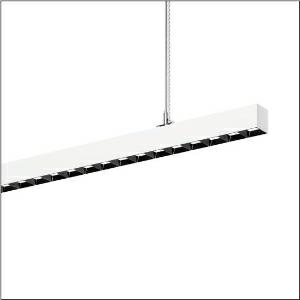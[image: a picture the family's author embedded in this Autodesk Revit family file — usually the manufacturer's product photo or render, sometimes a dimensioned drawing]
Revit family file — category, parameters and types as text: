
# Revit family: silica_r__21_51mx31dc4dwb_7dad
name_source: partatom
category: Lighting Fixtures
units: mm (PartAtom-declared; Revit-internal decimal feet)

## family parameters
Cut with Voids When Loaded = No
Host = Face
Light Source = No
Part Type = Normal
Room Calculation Point = No
Round Connector Dimension = Use Diameter
Shared = No

## types (1)
- --- (1 x LED, 18230 lm, 105.9 W, 4000K)
    Apparent Load = 106 VA
    CIE Flux Codes = 87 99 100 59 100
    Color Rendering = 80
    Color Temperature = 4000K
    Default Elevation = 1800 mm
    Description = Silica® 21, office luminaire, primary light control with darklight reflector, of PMMA, black, CAT 2 (L<= 3000cd/m²), light emission: direct/indirect distribution, primary light characteristic: symmetric, installation type: suspended mounting, LED, rated luminous flux: 18.230lm, luminous efficacy: 172lm/W, light colour: 840, colour temperature: 4000K, control gear: DALI 2, with terminal, 3+2-pole, max. 2.5mm², mains connection: 220..240V, AC, 50/60Hz, rated input power: 105.9W, luminaire housing, of aluminium, traffic white (RAL 9016), length: 3.004mm, width: 53mm, height: 53mm, protection rating (complete): IP20, insulation class (complete): insulation class I (protective earthing), certification: CE, permissible operating ambient temperature: 0..+35°C, standard: EN 50419, packaging unit: 1 piece
    Height = 53 mm
    Lamp = 1 x LED
    Lamp Light Flux = 18230 lm
    Lamp Power = 105.9 W
    Lamp count = 1
    Length = 3004 mm
    Luminous efficacy = 172 lm/W
    Manufacturer = Siteco
    ModVariant = No
    Model = 51MX31DC4DWB
    Mounting Place = Ceiling
    Mounting Type = Pendant
    Number of Poles = 1
    OnlyDefault = Yes
    Power Factor = 1
    Product Name = Silica® 21
    Product group = office luminaire | ceiling pendant
    ProductGroupID = 904
    Protection Class = Protection class I
    Protection Degree = IP 20
    RLX_Detail_Level = 1
    RLX_Emergency_Light_Flux = 0 lm
    RLX_Emergency_Type = 0
    RLX_Emergency_Type_DB = No
    RlxData = <blob elided: 64357 chars, md5=28e3a756>
    Socket = socket
    Standby Power = 0 W
    System Light Flux = 18230 lm
    System Power = 106 W
    Type Comments = factory setting: luminous flux: 100 % | dim-lin: 254 | 367 mA
    Type Image = l_1335871.jpg
    URL = http://relux.com
    VarID = @adj_121228
    Voltage = 0 V
    Weight = 0.00 kg
    Width = 53 mm

## geometry (parser evidence)
native form markers: Blend x4, Sweep x11
no freeform markers — native parametric forms only
